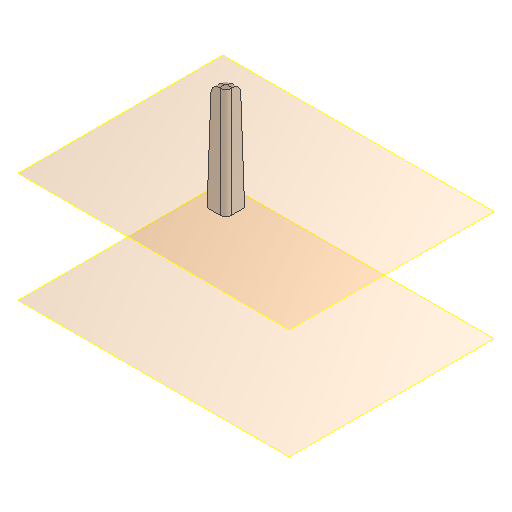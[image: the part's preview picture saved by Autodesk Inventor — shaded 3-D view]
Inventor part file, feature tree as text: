
AUTODESK INVENTOR PART (.ipt)
format: ipt  version: 2024.1 (Build 281209000, 209)  size: 159,744 bytes
history: native  units: mm
features: reference x4, sketch x3, plane x2, other x2, loft x1, extrude x1, fillet x1
ambient origin geometry x8: Origin, YZ Plane, XZ Plane, XY Plane, X Axis, Y Axis, Z Axis, Center Point
bodies: Body1 (feature_tree)
feature tree (14):
  plane  "Arbeitsebene1"
  sketch  "Skizze1"  dims[d0=10.0mm d1=2.0mm]
  plane  "Arbeitsebene2"
  loft  "Erhebung1"
  extrude  "Extrusion4"  TaperAngle=0.0deg  [1 undecoded]
  fillet  "Rundung1"  [1 undecoded]
  reference  "Referenz1"
  sketch  "Skizze4"  dims[d8=4.0mm d9=0.0mm d10=90.0deg d11=0.0mm d12=90.0deg]
  sketch  "Skizze5"  dims[d13=60.0mm d14=0.0mm d15=8.0mm d16=105.7mm]
  reference  "Referenz2"
  reference  "Referenz3"
  reference  "Referenz4"
  other  "Assembly_Planktoscope_Uc2version_wormdrive_V3.iam"
  other  "60_Planktoscope_MicroscopeHolder_Bottom_v0:1"
note: 2 required parameter values undecoded (feature->parameter linkage not recoverable at this tier; creation-order binding heuristic only, values carry confidence <= 0.55)
